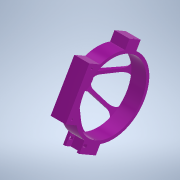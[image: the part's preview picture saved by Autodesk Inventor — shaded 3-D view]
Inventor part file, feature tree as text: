
AUTODESK INVENTOR PART (.ipt)
format: ipt  version: 2020.3 (Build 243373000, 373)  size: 462,336 bytes
history: native  units: mm
features: extrude x15, sketch x15, other x9, plane x6, projected_geometry x3, reference x3, pattern_circular x2, fillet x2
ambient origin geometry x8: Origin, YZ Plane, XZ Plane, XY Plane, X Axis, Y Axis, Z Axis, Center Point
bodies: Solid1 (feature_tree)
feature tree (55):
  other  "Prindere"
  other  "Blocks"
  extrude  "Extrusion1"  Depth=4.0mm
  plane  "Work Plane1"
  sketch  "Sketch3"  dims[d2=4.0mm d3=4.0mm]
  plane  "Work Plane2"
  extrude  "Extrusion2"  Depth=4.0mm
  pattern_circular  "Circular Pattern1"  Count=3  [1 undecoded]
  extrude  "Extrusion3"  Depth=67.5mm TaperAngle=0.0deg
  extrude  "Extrusion4"  Depth=30.0mm
  fillet  "Fillet1"  [1 undecoded]
  fillet  "Fillet2"  Radius=6.0mm
  extrude  "Extrusion6"  Depth=10.0mm
  plane  "Work Plane3"
  extrude  "Extrusion7"  Depth=10.0mm
  pattern_circular  "Circular Pattern2"  Count=3  [1 undecoded]
  extrude  "Extrusion8"  Depth=8.0mm
  extrude  "Extrusion9"  Depth=4.0mm
  extrude  "Extrusion10"  Depth=4.0mm
  sketch  "Sketch13"  dims[d25=10.0mm d26=0.0mm]
  plane  "Work Plane6"
  extrude  "Extrusion11"  Depth=8.0mm
  sketch  "Sketch14"  dims[d27=15.0deg]
  plane  "Work Plane7"
  extrude  "Extrusion12"  Depth=8.0mm
  sketch  "Sketch15"  dims[d28=6.5mm]
  plane  "Work Plane8"
  extrude  "Extrusion13"  Depth=8.0mm
  extrude  "Extrusion14"  Depth=40.0mm TaperAngle=0.0deg
  extrude  "Extrusion15"  Depth=10.0mm
  extrude  "Extrusion16"  Depth=2.5mm
  sketch  "Sketch1"  dims[d0=45.0mm d1=4.0mm]
  other  "Work Axis1"
  other  "Work Axis2"
  sketch  "Sketch5"  dims[d4=4.0mm]
  sketch  "Sketch6"  dims[d5=12.0mm]
  sketch  "Sketch8"  dims[d6=10.0mm d7=0.0mm d8=30.0mm]
  other  "Work Axis3"
  sketch  "Sketch9"  dims[d9=67.5mm d10=6.0mm d11=0.0mm]
  sketch  "Sketch10"  dims[d12=60.0mm d13=360.0deg d15=30.0mm d16=0.0mm d17=6.0mm]
  sketch  "Sketch11"  dims[d18=60.0mm d19=0.0mm d20=10.0mm]
  sketch  "Sketch12"  dims[d21=10.0mm d24=90.0mm]
  projected_geometry  "Projected Loop2"
  sketch  "Sketch16"  dims[d29=1.5mm d30=30.0mm d31=0.0mm]
  reference  "Reference2"
  reference  "Reference3"
  sketch  "Sketch17"  dims[d33=20.0mm d34=360.0deg d36=8.0mm]
  projected_geometry  "Projected Loop3"
  projected_geometry  "Projected Loop4"
  sketch  "Sketch18"  dims[d37=10.0mm d38=0.0mm d39=4.0mm d40=4.0mm d41=8.0mm d42=8.0mm d43=8.0mm d44=40.0mm d45=0.0mm d47=10.0mm d48=2.5mm d49=3.0mm d50=0.0mm d51=0.0mm d52=11.75mm d53=0.0mm d54=4.0mm d55=10.0mm d56=0.0mm d57=10.0mm d58=0.0mm d59=2.5mm d60=2.5mm d61=10.0mm d62=0.0mm d63=4.25mm d64=0.0mm d65=5.0mm d66=8.0mm d67=37.6mm d68=0.0mm]
  reference  "Reference4"
  other  "Prindere:1"
  other  "<userpath>\Documents\Inventor\TheArch\R&D\Beta0\Structura\Prototip\Prototip1.iam"
  other  "Prototip1.iam"
  other  "SG90:1"
note: 3 required parameter values undecoded (feature->parameter linkage not recoverable at this tier; creation-order binding heuristic only, values carry confidence <= 0.55)
